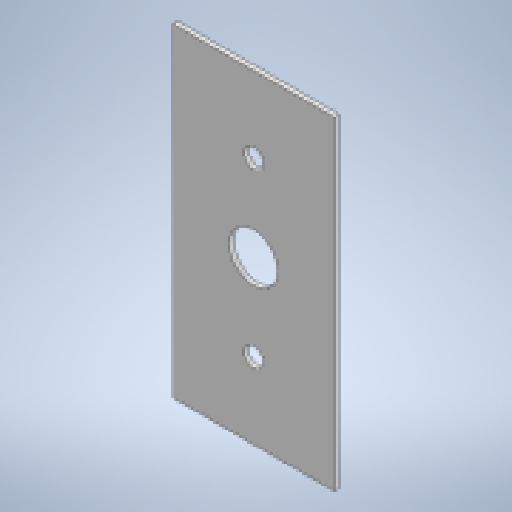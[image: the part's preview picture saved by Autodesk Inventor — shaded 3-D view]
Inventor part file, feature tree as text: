
AUTODESK INVENTOR PART (.ipt)
format: ipt  version: 2024 (Build 280153000, 153)  size: 187,904 bytes
history: native  units: mm
features: reference x15, other x7, extrude x2, sketch x2
ambient origin geometry x8: Origin, YZ Plane, XZ Plane, XY Plane, X Axis, Y Axis, Z Axis, Center Point
bodies: Body1 (feature_tree)
feature tree (26):
  other  "ソリッド1"
  extrude  "押し出し1"  Depth=6.0mm
  extrude  "押し出し2"  Depth=6.0mm
  sketch  "スケッチ1"
  reference  "参照1"
  reference  "参照2"
  reference  "参照3"
  sketch  "スケッチ2"
  reference  "参照4"
  reference  "参照5"
  reference  "参照6"
  reference  "参照7"
  reference  "参照8"
  reference  "参照9"
  reference  "参照10"
  reference  "参照11"
  reference  "参照12"
  reference  "参照13"
  reference  "参照14"
  reference  "参照15"
  other  "<userpath>\OneDrive\ドキュメント\Inventor\Vixen\kosi.iam"
  other  "kosi.iam"
  other  "gia1:1"
  other  "gia1:2"
  other  "kosipitch:1"
  other  "kosipitch:2"
